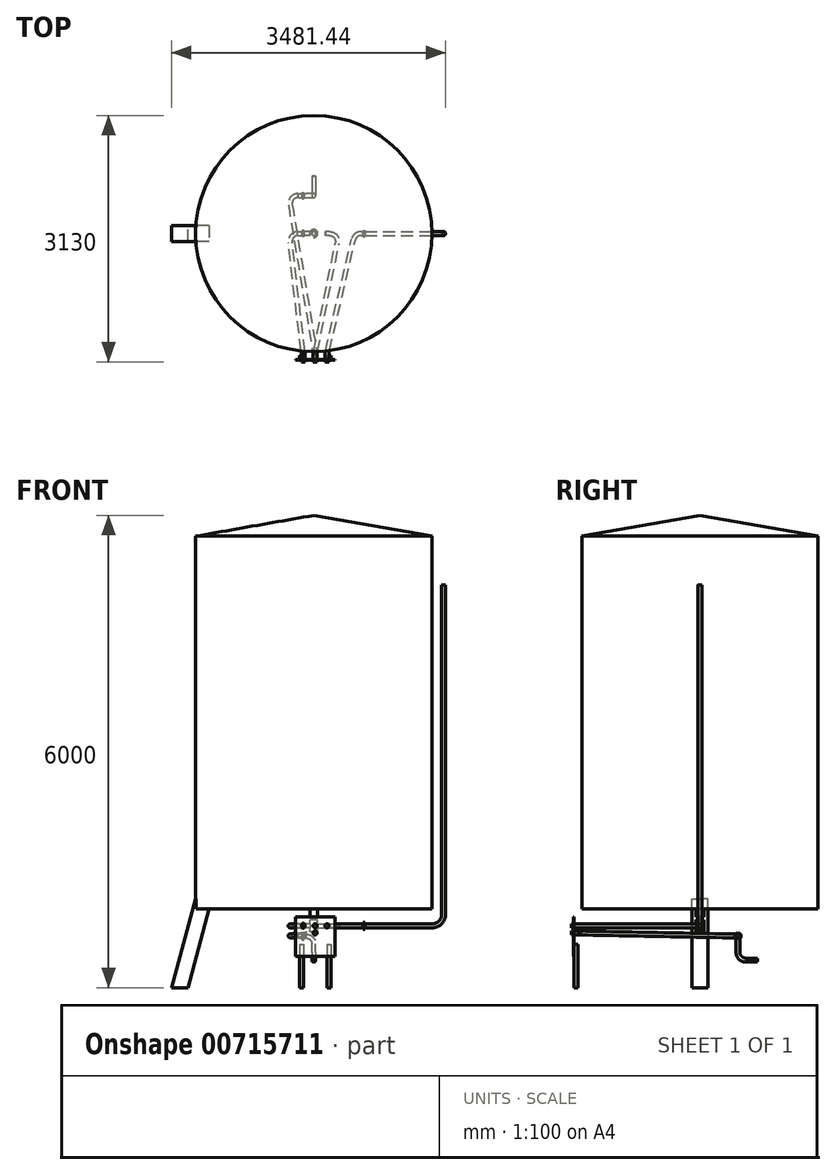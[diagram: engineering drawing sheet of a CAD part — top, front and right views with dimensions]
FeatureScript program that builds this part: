
annotation { "Feature Type Name" : "Feature", "Feature Type Description" : "" }
export const myFeature = defineFeature(function(context is Context, id is Id, definition is map)
    precondition{}
    {
        {
            var Q0;
            Q0=qCreatedBy(makeId("Front.planeOp"),FACE);
            var sketch = newSketch(context, id + "F0", { "sketchPlane" : qUnion([Q0])});
            skLineSegment(sketch, "E0", {"start": v(0, 5290) * mm, "end": v(0, 0) * mm});
            skLineSegment(sketch, "E1", {"start": v(0, 5290) * mm, "end": v(-1500, 5025.5) * mm});
            skLineSegment(sketch, "E2", {"start": v(-1500, 5025.5) * mm, "end": v(-1500, 290) * mm});
            skLineSegment(sketch, "E3", {"start": v(-1500, 290) * mm, "end": v(-50, 290) * mm});
            skLineSegment(sketch, "E4", {"start": v(-50, 290) * mm, "end": v(-50, 190) * mm});
            skLineSegment(sketch, "E5", {"start": v(-25, 190) * mm, "end": v(-50, 190) * mm});
            skLineSegment(sketch, "E6", {"start": v(-50, 0) * mm, "end": v(0, 0) * mm});
            skLineSegment(sketch, "E7", {"start": v(-50, 150) * mm, "end": v(-50, 0) * mm});
            skLineSegment(sketch, "E8", {"start": v(-25, 190) * mm, "end": v(-25, 150) * mm});
            skLineSegment(sketch, "E9", {"start": v(-25, 150) * mm, "end": v(-50, 150) * mm});
            skSolve(sketch);
        }
        {
            var Q0;
            Q0=makeQuery(id+"F0.imprint","IMPRINT",FACE,{"disambiguationData":[TD([[makeQuery(id+"F0.imprint","IMPRINT",EDGE,{"derivedFrom":sQuery(id+"F0.wireOp",EDGE,"E0")}),-1.0]])]});
            var Q1;
            Q1=sQuery(id+"F0.wireOp",EDGE,"E0");
            revolve(context, id + "F1", {"surfaceOperationType" : NewSurfaceOperationType.NEW, "entities" : qUnion([Q0]), "axis" : qUnion([Q1]), "revolveType" : RevolveType.FULL});
        }
        {
            var Q0;
            Q0=qCreatedBy(makeId("Front.planeOp"),FACE);
            var sketch = newSketch(context, id + "F2", { "sketchPlane" : qUnion([Q0])});
            skLineSegment(sketch, "E10", {"start": v(-1500, 5025.5) * mm, "end": v(-1500, 290) * mm, "construction": true});
            skLineSegment(sketch, "E11", {"start": v(1500, 290) * mm, "end": v(1500, 5025.5) * mm});
            skLineSegment(sketch, "E12", {"start": v(50, 290) * mm, "end": v(1500, 290) * mm});
            skLineSegment(sketch, "E13", {"start": v(-1500, 290) * mm, "end": v(-50, 290) * mm, "construction": true});
            skLineSegment(sketch, "E14", {"start": v(-1806.44, -710) * mm, "end": v(-1505, 415) * mm});
            skLineSegment(sketch, "E15", {"start": v(-1297.94, 415) * mm, "end": v(-1599.39, -710) * mm});
            skLineSegment(sketch, "E16", {"start": v(-1599.39, -710) * mm, "end": v(-1806.44, -710) * mm});
            skLineSegment(sketch, "E17", {"start": v(-1505, 415) * mm, "end": v(-1297.94, 415) * mm});
            skSolve(sketch);
        }
        {
            var Q0;
            Q0=makeQuery(id+"F2.imprint","IMPRINT",FACE,{"disambiguationData":[TD([[makeQuery(id+"F2.imprint","IMPRINT",EDGE,{"derivedFrom":sQuery(id+"F2.wireOp",EDGE,"E14")}),-1.0]])]});
            extrude(context, id + "F3", {"entities" : qUnion([Q0]), "operationType" : NewBodyOperationType.ADD, "endBound" : BoundingType.SYMMETRIC, "depth" : 200 * mm, "offsetDistance" : 25 * mm});
        }
        {
            var Q0;
            Q0=qCreatedBy(makeId("Right.planeOp"),FACE);
            cPlane(context, id + "F4", {"entities" : qUnion([Q0]), "cplaneType" : CPlaneType.OFFSET, "offset" : 150 * mm, "oppositeDirection" : true, "width" : 150 * mm, "height" : 150 * mm});
        }
        {
            var Q0;
            Q0=qCreatedBy(id+"F4.planeOp",FACE);
            var sketch = newSketch(context, id + "F5", { "sketchPlane" : qUnion([Q0])});
            skLineSegment(sketch, "E18", {"start": v(0, 0) * mm, "end": v(0, 150) * mm, "construction": true});
            skLineSegment(sketch, "E19.0", {"start": v(-50, 150) * mm, "end": v(50, 150) * mm, "construction": true});
            skLineSegment(sketch, "E20.0", {"start": v(-50, 0) * mm, "end": v(50, 0) * mm, "construction": true});
            skCircle(sketch, "E21", {"center": v(0, 75) * mm, "radius": 25 * mm});
            skCircle(sketch, "E22.cCircle", {"center": v(0, 75) * mm, "radius": 40 * mm, "construction": true});
            skLineSegment(sketch, "E22.0", {"start": v(-40, 51.9) * mm, "end": v(-40, 98.1) * mm});
            skLineSegment(sketch, "E22.1", {"start": v(-40, 98.1) * mm, "end": v(0, 121.19) * mm});
            skLineSegment(sketch, "E22.2", {"start": v(0, 121.19) * mm, "end": v(40, 98.1) * mm});
            skLineSegment(sketch, "E22.3", {"start": v(40, 98.1) * mm, "end": v(40, 51.9) * mm});
            skLineSegment(sketch, "E22.4", {"start": v(40, 51.9) * mm, "end": v(0, 28.81) * mm});
            skLineSegment(sketch, "E22.5", {"start": v(0, 28.81) * mm, "end": v(-40, 51.9) * mm});
            skPoint(sketch, "E22.0.midPoint", {"position": v(-40, 75) * mm});
            skSolve(sketch);
        }
        {
            var Q0;
            Q0=makeQuery(id+"F5.imprint","IMPRINT",FACE,{"disambiguationData":[TD([[makeQuery(id+"F5.imprint","IMPRINT",EDGE,{"derivedFrom":sQuery(id+"F5.wireOp",EDGE,"E21")}),-1.0]])]});
            var Q1;
            Q1=makeQuery(id+"F5.imprint","IMPRINT",FACE,{"disambiguationData":[TD([[makeQuery(id+"F5.imprint","IMPRINT",EDGE,{"derivedFrom":sQuery(id+"F5.wireOp",EDGE,"E21")}),1.0]])]});
            extrude(context, id + "F6", {"entities" : qUnion([Q0, Q1]), "depth" : 25 * mm, "offsetDistance" : 25 * mm});
        }
        {
            var Q0;
            Q0=makeQuery(id+"F5.imprint","IMPRINT",FACE,{"disambiguationData":[TD([[makeQuery(id+"F5.imprint","IMPRINT",EDGE,{"derivedFrom":sQuery(id+"F5.wireOp",EDGE,"E21")}),1.0]])]});
            var Q1;
            Q1=makeQuery(id+"F1.opRevolve","SWEPT_FACE",FACE,{"disambiguationData":[OSD([sQuery(id+"F0.wireOp",EDGE,"E7")])]});
            extrude(context, id + "F7", {"entities" : qUnion([Q0]), "operationType" : NewBodyOperationType.ADD, "endBound" : BoundingType.UP_TO_SURFACE, "depth" : 25 * mm, "endBoundEntityFace" : qUnion([Q1]), "offsetDistance" : 25 * mm});
        }
        {
            var Q0;
            Q0=qCreatedBy(makeId("Front.planeOp"),FACE);
            var sketch = newSketch(context, id + "F8", { "sketchPlane" : qUnion([Q0])});
            skLineSegment(sketch, "E23.0.0", {"start": v(150, 51.9) * mm, "end": v(150, 28.81) * mm, "construction": true});
            skLineSegment(sketch, "E23.0.1", {"start": v(150, 28.81) * mm, "end": v(150, 51.9) * mm, "construction": true});
            skLineSegment(sketch, "E23.0.2", {"start": v(150, 51.9) * mm, "end": v(150, 98.1) * mm, "construction": true});
            skLineSegment(sketch, "E23.0.3", {"start": v(150, 98.1) * mm, "end": v(150, 121.19) * mm, "construction": true});
            skLineSegment(sketch, "E23.0.4", {"start": v(150, 121.19) * mm, "end": v(150, 98.1) * mm, "construction": true});
            skLineSegment(sketch, "E23.0.5", {"start": v(150, 98.1) * mm, "end": v(150, 51.9) * mm, "construction": true});
            skLineSegment(sketch, "E24", {"start": v(150, 75) * mm, "end": v(650, 75) * mm, "construction": true});
            skLineSegment(sketch, "E25", {"start": v(1650, 225) * mm, "end": v(1650, 4408.12) * mm});
            skPoint(sketch, "E26.visualSharp", {"position": v(1650, 75) * mm});
            skArc(sketch, "E26.filletArc", {"start": v(1500, 75) * mm, "mid": v(1606.07, 118.93) * mm, "end": v(1650, 225) * mm});
            skPoint(sketch, "E27", {"position": v(650, 75) * mm});
            skLineSegment(sketch, "E28", {"start": v(650, 75) * mm, "end": v(1500, 75) * mm});
            skPoint(sketch, "E29", {"position": v(675, 75) * mm});
            skSolve(sketch);
        }
        {
            var Q0;
            Q0=makeQuery(id+"F7.opExtrude","SWEPT_FACE",FACE,{"disambiguationData":[OSD([sQuery(id+"F5.wireOp",EDGE,"E21")])]});
            var Q1;
            Q1=qCreatedBy(makeId("Top.planeOp"),FACE);
            cPlane(context, id + "F9", {"entities" : qUnion([Q0, Q1]), "cplaneType" : CPlaneType.LINE_ANGLE, "offset" : 25 * mm, "angle" : 15 * degree, "width" : 150 * mm, "height" : 150 * mm});
        }
        {
            var Q0;
            Q0=qCreatedBy(id+"F9.planeOp",FACE);
            var sketch = newSketch(context, id + "F10", { "sketchPlane" : qUnion([Q0])});
            skPoint(sketch, "E30.0", {"position": v(-150, 19.41) * mm});
            skLineSegment(sketch, "E31", {"start": v(-150, 19.41) * mm, "end": v(-400, 19.41) * mm});
            skLineSegment(sketch, "E32", {"start": v(-500, -80.59) * mm, "end": v(-500, -380.59) * mm});
            skLineSegment(sketch, "E33", {"start": v(-400, -480.59) * mm, "end": v(-375, -480.59) * mm});
            skPoint(sketch, "E34.visualSharp", {"position": v(-500, 19.41) * mm});
            skArc(sketch, "E34.filletArc", {"start": v(-400, 19.41) * mm, "mid": v(-470.71, -9.88) * mm, "end": v(-500, -80.59) * mm});
            skPoint(sketch, "E35.visualSharp", {"position": v(-500, -480.59) * mm});
            skArc(sketch, "E35.filletArc", {"start": v(-500, -380.59) * mm, "mid": v(-470.71, -451.3) * mm, "end": v(-400, -480.59) * mm});
            skSolve(sketch);
        }
        {
            var Q0;
            Q0=qCreatedBy(makeId("Front.planeOp"),FACE);
            var Q1;
            Q1=sQuery(id+"F10.wireOp",VERTEX,"E33.end");
            cPlane(context, id + "F11", {"entities" : qUnion([Q0, Q1]), "cplaneType" : CPlaneType.PLANE_POINT, "offset" : 25 * mm, "width" : 150 * mm, "height" : 150 * mm});
        }
        {
            var Q0;
            Q0=qCreatedBy(id+"F11.planeOp",FACE);
            var sketch = newSketch(context, id + "F12", { "sketchPlane" : qUnion([Q0])});
            skLineSegment(sketch, "E36", {"start": v(0, -154.4) * mm, "end": v(0, -204.4) * mm});
            skPoint(sketch, "E37.0", {"position": v(-375, -54.4) * mm});
            skLineSegment(sketch, "E38", {"start": v(-375, -54.4) * mm, "end": v(-125, -54.4) * mm, "construction": true});
            skPoint(sketch, "E39.visualSharp", {"position": v(0, -54.4) * mm});
            skArc(sketch, "E39.filletArc", {"start": v(0, -154.4) * mm, "mid": v(-29.29, -83.7) * mm, "end": v(-100, -54.4) * mm});
            skPoint(sketch, "E40", {"position": v(-125, -54.4) * mm});
            skLineSegment(sketch, "E41", {"start": v(-125, -54.4) * mm, "end": v(-100, -54.4) * mm});
            skSolve(sketch);
        }
        {
            var Q0;
            Q0=qCreatedBy(makeId("Right.planeOp"),FACE);
            var sketch = newSketch(context, id + "F13", { "sketchPlane" : qUnion([Q0])});
            skLineSegment(sketch, "E42", {"start": v(582.96, -360) * mm, "end": v(732.96, -360) * mm});
            skPoint(sketch, "E43.0", {"position": v(482.96, -204.4) * mm});
            skLineSegment(sketch, "E44", {"start": v(482.96, -204.4) * mm, "end": v(482.96, -260) * mm});
            skPoint(sketch, "E45.visualSharp", {"position": v(482.96, -360) * mm});
            skArc(sketch, "E45.filletArc", {"start": v(482.96, -260) * mm, "mid": v(512.25, -330.71) * mm, "end": v(582.96, -360) * mm});
            skSolve(sketch);
        }
        {
            var Q0;
            Q0=sQuery(id+"F13.wireOp",VERTEX,"E42.end");
            var Q1;
            Q1=sQuery(id+"F13.wireOp",EDGE,"E42");
            cPlane(context, id + "F14", {"entities" : qUnion([Q0, Q1]), "cplaneType" : CPlaneType.LINE_POINT, "offset" : 25 * mm, "width" : 150 * mm, "height" : 150 * mm});
        }
        {
            var Q0;
            Q0=qCreatedBy(id+"F14.planeOp",FACE);
            var sketch = newSketch(context, id + "F15", { "sketchPlane" : qUnion([Q0])});
            skCircle(sketch, "E46", {"center": v(0, -360) * mm, "radius": 25 * mm});
            skSolve(sketch);
        }
        {
            var Q0;
            Q0=sQuery(id+"F8.wireOp",VERTEX,"E25.end");
            var Q1;
            Q1=sQuery(id+"F8.wireOp",EDGE,"E25");
            cPlane(context, id + "F16", {"entities" : qUnion([Q0, Q1]), "cplaneType" : CPlaneType.LINE_POINT, "offset" : 25 * mm, "width" : 150 * mm, "height" : 150 * mm});
        }
        {
            var Q0;
            Q0=qCreatedBy(id+"F16.planeOp",FACE);
            var sketch = newSketch(context, id + "F17", { "sketchPlane" : qUnion([Q0])});
            skPoint(sketch, "E47.0", {"position": v(1650, 0) * mm});
            skCircle(sketch, "E48", {"center": v(1650, 0) * mm, "radius": 25 * mm});
            skSolve(sketch);
        }
        {
            var Q0;
            Q0=makeQuery(id+"F17.imprint","IMPRINT",FACE,{"disambiguationData":[TD([[makeQuery(id+"F17.imprint","IMPRINT",EDGE,{"derivedFrom":sQuery(id+"F17.wireOp",EDGE,"E48")}),1.0]])]});
            var Q1;
            Q1=sQuery(id+"F8.wireOp",EDGE,"E25");
            var Q2;
            Q2=sQuery(id+"F8.wireOp",EDGE,"E26.filletArc");
            var Q3;
            Q3=sQuery(id+"F8.wireOp",EDGE,"E24");
            sweep(context, id + "F18", {"operationType" : NewBodyOperationType.ADD, "profiles" : qUnion([Q0]), "path" : qUnion([Q1, Q2, Q3])});
        }
        {
            var Q0;
            Q0=makeQuery(id+"F15.imprint","IMPRINT",FACE,{"disambiguationData":[TD([[makeQuery(id+"F15.imprint","IMPRINT",EDGE,{"derivedFrom":sQuery(id+"F15.wireOp",EDGE,"E46")}),1.0]])]});
            var Q1;
            Q1=sQuery(id+"F13.wireOp",EDGE,"E42");
            var Q2;
            Q2=sQuery(id+"F13.wireOp",EDGE,"E45.filletArc");
            var Q3;
            Q3=sQuery(id+"F13.wireOp",EDGE,"E44");
            var Q4;
            Q4=sQuery(id+"F12.wireOp",EDGE,"E36");
            var Q5;
            Q5=sQuery(id+"F12.wireOp",EDGE,"E39.filletArc");
            sweep(context, id + "F19", {"operationType" : NewBodyOperationType.ADD, "profiles" : qUnion([Q0]), "path" : qUnion([Q1, Q2, Q3, Q4, Q5])});
        }
        {
            var Q0;
            Q0=sQuery(id+"F12.wireOp",VERTEX,"E40");
            var Q1;
            Q1=sQuery(id+"F12.wireOp",EDGE,"E38");
            cPlane(context, id + "F20", {"entities" : qUnion([Q0, Q1]), "cplaneType" : CPlaneType.LINE_POINT, "offset" : 25 * mm, "width" : 150 * mm, "height" : 150 * mm});
        }
        {
            var Q0;
            Q0=qCreatedBy(id+"F20.planeOp",FACE);
            var sketch = newSketch(context, id + "F21", { "sketchPlane" : qUnion([Q0])});
            skPoint(sketch, "E49.0", {"position": v(482.96, -54.4) * mm});
            skCircle(sketch, "E50.cCircle", {"center": v(482.96, -54.4) * mm, "radius": 40 * mm, "construction": true});
            skLineSegment(sketch, "E50.0", {"start": v(522.96, -31.32) * mm, "end": v(522.96, -77.5) * mm});
            skLineSegment(sketch, "E50.1", {"start": v(522.96, -77.5) * mm, "end": v(482.96, -100.6) * mm});
            skLineSegment(sketch, "E50.2", {"start": v(482.96, -100.6) * mm, "end": v(442.96, -77.5) * mm});
            skLineSegment(sketch, "E50.3", {"start": v(442.96, -77.5) * mm, "end": v(442.96, -31.32) * mm});
            skLineSegment(sketch, "E50.4", {"start": v(442.96, -31.32) * mm, "end": v(482.96, -8.22) * mm});
            skLineSegment(sketch, "E50.5", {"start": v(482.96, -8.22) * mm, "end": v(522.96, -31.32) * mm});
            skPoint(sketch, "E50.0.midPoint", {"position": v(522.96, -54.4) * mm});
            skSolve(sketch);
        }
        {
            var Q0;
            Q0=makeQuery(id+"F21.imprint","IMPRINT",FACE,{"disambiguationData":[TD([[makeQuery(id+"F21.imprint","IMPRINT",EDGE,{"derivedFrom":sQuery(id+"F21.wireOp",EDGE,"E50.0")}),-1.0]])]});
            extrude(context, id + "F22", {"entities" : qUnion([Q0]), "operationType" : NewBodyOperationType.ADD, "oppositeDirection" : true, "depth" : 25 * mm, "offsetDistance" : 25 * mm});
        }
        {
            var Q0;
            Q0=qCreatedBy(makeId("Front.planeOp"),FACE);
            cPlane(context, id + "F23", {"entities" : qUnion([Q0]), "cplaneType" : CPlaneType.OFFSET, "offset" : 1600 * mm, "width" : 150 * mm, "height" : 150 * mm});
        }
        {
            var Q0;
            Q0=qCreatedBy(id+"F23.planeOp",FACE);
            var sketch = newSketch(context, id + "F24", { "sketchPlane" : qUnion([Q0])});
            skLineSegment(sketch, "E51.bottom", {"start": v(-233.38, 190) * mm, "end": v(266.62, 190) * mm});
            skLineSegment(sketch, "E51.top", {"start": v(-233.38, -310) * mm, "end": v(266.62, -310) * mm});
            skLineSegment(sketch, "E51.left", {"start": v(-233.38, 190) * mm, "end": v(-233.38, -310) * mm});
            skLineSegment(sketch, "E51.right", {"start": v(266.62, 190) * mm, "end": v(266.62, -310) * mm});
            skLineSegment(sketch, "E52.bottom", {"start": v(-183.38, -160) * mm, "end": v(-133.38, -160) * mm});
            skLineSegment(sketch, "E52.top", {"start": v(-183.38, -710) * mm, "end": v(-133.38, -710) * mm});
            skLineSegment(sketch, "E52.left", {"start": v(-183.38, -160) * mm, "end": v(-183.38, -710) * mm});
            skLineSegment(sketch, "E52.right", {"start": v(-133.38, -160) * mm, "end": v(-133.38, -710) * mm});
            skLineSegment(sketch, "E53.bottom", {"start": v(166.62, -160) * mm, "end": v(216.62, -160) * mm});
            skLineSegment(sketch, "E53.top", {"start": v(166.62, -710) * mm, "end": v(216.62, -710) * mm});
            skLineSegment(sketch, "E53.left", {"start": v(166.62, -160) * mm, "end": v(166.62, -710) * mm});
            skLineSegment(sketch, "E53.right", {"start": v(216.62, -160) * mm, "end": v(216.62, -710) * mm});
            skSolve(sketch);
        }
        {
            var Q0;
            Q0=makeQuery(id+"F24.imprint","IMPRINT",FACE,{"disambiguationData":[TD([[makeQuery(id+"F24.imprint","IMPRINT",EDGE,{"derivedFrom":sQuery(id+"F24.wireOp",EDGE,"E51.bottom")}),-1.0]])]});
            var Q1;
            {var subQ5=sQuery(id+"F24.wireOp",EDGE,"E52.bottom");Q1=makeQuery(id+"F24.imprint","IMPRINT",FACE,{"disambiguationData":[TD([[makeQuery(id+"F24.imprint","IMPRINT",EDGE,{"derivedFrom":subQ5}),-1.0]])]});}
            var Q2;
            {var subQ5=sQuery(id+"F24.wireOp",EDGE,"E53.bottom");Q2=makeQuery(id+"F24.imprint","IMPRINT",FACE,{"disambiguationData":[TD([[makeQuery(id+"F24.imprint","IMPRINT",EDGE,{"derivedFrom":subQ5}),-1.0]])]});}
            extrude(context, id + "F25", {"entities" : qUnion([Q0, Q1, Q2]), "depth" : 5 * mm, "offsetDistance" : 25 * mm});
        }
        {
            var Q0;
            {var subQ5=sQuery(id+"F24.wireOp",EDGE,"E52.top");Q0=makeQuery(id+"F24.imprint","IMPRINT",FACE,{"disambiguationData":[TD([[makeQuery(id+"F24.imprint","IMPRINT",EDGE,{"derivedFrom":subQ5}),1.0]])]});}
            var Q1;
            {var subQ5=sQuery(id+"F24.wireOp",EDGE,"E53.top");Q1=makeQuery(id+"F24.imprint","IMPRINT",FACE,{"disambiguationData":[TD([[makeQuery(id+"F24.imprint","IMPRINT",EDGE,{"derivedFrom":subQ5}),1.0]])]});}
            var Q2;
            {var subQ5=sQuery(id+"F24.wireOp",EDGE,"E52.bottom");Q2=makeQuery(id+"F24.imprint","IMPRINT",FACE,{"disambiguationData":[TD([[makeQuery(id+"F24.imprint","IMPRINT",EDGE,{"derivedFrom":subQ5}),-1.0]])]});}
            var Q3;
            {var subQ5=sQuery(id+"F24.wireOp",EDGE,"E53.bottom");Q3=makeQuery(id+"F24.imprint","IMPRINT",FACE,{"disambiguationData":[TD([[makeQuery(id+"F24.imprint","IMPRINT",EDGE,{"derivedFrom":subQ5}),-1.0]])]});}
            extrude(context, id + "F26", {"entities" : qUnion([Q0, Q1, Q2, Q3]), "operationType" : NewBodyOperationType.ADD, "oppositeDirection" : true, "depth" : 50 * mm, "offsetDistance" : 25 * mm});
        }
        {
            var Q0;
            Q0=makeQuery(id+"F19.opSweep","CAP_FACE",FACE,{"disambiguationData":[OSD([sQuery(id+"F12.wireOp",VERTEX,"E39.filletArc.end"),sQuery(id+"F15.wireOp",EDGE,"E46")])],"isStart":false});
            extrude(context, id + "F27", {"entities" : qUnion([Q0]), "operationType" : NewBodyOperationType.ADD, "endBound" : BoundingType.UP_TO_NEXT, "depth" : 25 * mm, "offsetDistance" : 25 * mm});
        }
        {
            var Q0;
            Q0=qCreatedBy(makeId("Top.planeOp"),FACE);
            var Q1;
            Q1=sQuery(id+"F8.wireOp",VERTEX,"E27");
            cPlane(context, id + "F28", {"entities" : qUnion([Q0, Q1]), "cplaneType" : CPlaneType.PLANE_POINT, "offset" : 25 * mm, "width" : 150 * mm, "height" : 150 * mm});
        }
        {
            var Q0;
            Q0=qCreatedBy(id+"F28.planeOp",FACE);
            var sketch = newSketch(context, id + "F29", { "sketchPlane" : qUnion([Q0])});
            skPoint(sketch, "E54.0", {"position": v(650, 0) * mm});
            skLineSegment(sketch, "E55", {"start": v(650, 0) * mm, "end": v(600, 0) * mm});
            skLineSegment(sketch, "E56", {"start": v(502.61, -77.3) * mm, "end": v(169.23, -1507.3) * mm});
            skLineSegment(sketch, "E57.0", {"start": v(-233.38, -1600) * mm, "end": v(266.62, -1600) * mm, "construction": true});
            skLineSegment(sketch, "E58", {"start": v(166.62, -1630) * mm, "end": v(166.62, -1530) * mm});
            skPoint(sketch, "E59.visualSharp", {"position": v(166.62, -1518.5) * mm});
            skArc(sketch, "E59.filletArc", {"start": v(169.23, -1507.3) * mm, "mid": v(167.27, -1518.57) * mm, "end": v(166.62, -1530) * mm});
            skPoint(sketch, "E60.visualSharp", {"position": v(520.63, 0) * mm});
            skArc(sketch, "E60.filletArc", {"start": v(600, 0) * mm, "mid": v(537.83, -21.67) * mm, "end": v(502.61, -77.3) * mm});
            skLineSegment(sketch, "E61", {"start": v(16.62, -1630) * mm, "end": v(16.62, -1539.88) * mm});
            skLineSegment(sketch, "E62", {"start": v(18.55, -1520.31) * mm, "end": v(298.07, -119.57) * mm});
            skLineSegment(sketch, "E63", {"start": v(200, 0) * mm, "end": v(150, 0) * mm});
            skPoint(sketch, "E64.0", {"position": v(150, 0) * mm});
            skPoint(sketch, "E65.visualSharp", {"position": v(321.93, 0) * mm});
            skArc(sketch, "E65.filletArc", {"start": v(298.07, -119.57) * mm, "mid": v(277.32, -36.58) * mm, "end": v(200, 0) * mm});
            skPoint(sketch, "E66.0", {"position": v(-150, 0) * mm});
            skLineSegment(sketch, "E67", {"start": v(-150, 0) * mm, "end": v(-200, 0) * mm});
            skLineSegment(sketch, "E68", {"start": v(-299.32, -111.62) * mm, "end": v(-134.06, -1524.2) * mm});
            skLineSegment(sketch, "E69", {"start": v(-133.38, -1535.83) * mm, "end": v(-133.38, -1630) * mm});
            skPoint(sketch, "E70.visualSharp", {"position": v(-312.38, 0) * mm});
            skArc(sketch, "E70.filletArc", {"start": v(-200, 0) * mm, "mid": v(-274.7, -33.52) * mm, "end": v(-299.32, -111.62) * mm});
            skPoint(sketch, "E71.visualSharp", {"position": v(-133.38, -1530) * mm});
            skArc(sketch, "E71.filletArc", {"start": v(-133.38, -1535.83) * mm, "mid": v(-133.55, -1530) * mm, "end": v(-134.06, -1524.2) * mm});
            skPoint(sketch, "E72.visualSharp", {"position": v(16.62, -1530) * mm});
            skArc(sketch, "E72.filletArc", {"start": v(18.55, -1520.31) * mm, "mid": v(17.1, -1530.05) * mm, "end": v(16.62, -1539.88) * mm});
            skSolve(sketch);
        }
        {
            var Q0;
            Q0=makeQuery(id+"F25.opExtrude","CAP_FACE",FACE,{"disambiguationData":[OSD([sQuery(id+"F24.wireOp",EDGE,"E51.bottom"),sQuery(id+"F24.wireOp",EDGE,"E51.top"),sQuery(id+"F24.wireOp",EDGE,"E51.left"),sQuery(id+"F24.wireOp",EDGE,"E51.right")])],"isStart":false});
            cPlane(context, id + "F30", {"entities" : qUnion([Q0]), "cplaneType" : CPlaneType.OFFSET, "offset" : 25 * mm, "width" : 150 * mm, "height" : 150 * mm});
        }
        {
            var Q0;
            Q0=qCreatedBy(id+"F30.planeOp",FACE);
            var sketch = newSketch(context, id + "F31", { "sketchPlane" : qUnion([Q0])});
            skPoint(sketch, "E73.0", {"position": v(-133.38, 75) * mm});
            skPoint(sketch, "E74.0", {"position": v(16.62, 75) * mm});
            skPoint(sketch, "E75.0", {"position": v(166.62, 75) * mm});
            skPoint(sketch, "E76", {"position": v(16.62, -15.14) * mm});
            skCircle(sketch, "E77", {"center": v(-133.38, 75) * mm, "radius": 25 * mm});
            skCircle(sketch, "E78", {"center": v(16.62, -15.14) * mm, "radius": 25 * mm});
            skCircle(sketch, "E79", {"center": v(16.62, 75) * mm, "radius": 25 * mm});
            skCircle(sketch, "E80", {"center": v(166.62, 75) * mm, "radius": 25 * mm});
            skSolve(sketch);
        }
        {
            var Q0;
            Q0=makeQuery(id+"F31.imprint","IMPRINT",FACE,{"disambiguationData":[TD([[makeQuery(id+"F31.imprint","IMPRINT",EDGE,{"derivedFrom":sQuery(id+"F31.wireOp",EDGE,"E78")}),1.0]])]});
            var Q1;
            Q1=sQuery(id+"F29.wireOp",VERTEX,"E72.filletArc.end");
            extrude(context, id + "F32", {"entities" : qUnion([Q0]), "operationType" : NewBodyOperationType.ADD, "endBound" : BoundingType.UP_TO_VERTEX, "oppositeDirection" : true, "depth" : 25 * mm, "endBoundEntityVertex" : qUnion([Q1]), "offsetDistance" : 25 * mm});
        }
        {
            var Q0;
            Q0=makeQuery(id+"F32.opExtrude","CAP_FACE",FACE,{"disambiguationData":[OSD([sQuery(id+"F31.wireOp",EDGE,"E78")])],"isStart":false});
            var sketch = newSketch(context, id + "F33", { "sketchPlane" : qUnion([Q0])});
            skCircle(sketch, "E81.0", {"center": v(-16.62, -15.14) * mm, "radius": 25 * mm});
            skSolve(sketch);
        }
        {
            var Q0;
            Q0=sQuery(id+"F33.wireOp",VERTEX,"E81.0.center");
            var Q1;
            Q1=sQuery(id+"F12.wireOp",VERTEX,"E37.0");
            var Q2;
            Q2=sQuery(id+"F12.wireOp",VERTEX,"E40");
            cPlane(context, id + "F34", {"entities" : qUnion([Q0, Q1, Q2]), "cplaneType" : CPlaneType.THREE_POINT, "offset" : 25 * mm, "width" : 150 * mm, "height" : 150 * mm});
        }
        {
            var Q0;
            Q0=qCreatedBy(id+"F34.planeOp",FACE);
            var sketch = newSketch(context, id + "F35", { "sketchPlane" : qUnion([Q0])});
            skLineSegment(sketch, "E82.0.0", {"start": v(-150, 483.03) * mm, "end": v(-150, 523.47) * mm, "construction": true});
            skLineSegment(sketch, "E82.0.1", {"start": v(-150, 523.47) * mm, "end": v(-150, 524.37) * mm, "construction": true});
            skLineSegment(sketch, "E82.0.2", {"start": v(-150, 524.37) * mm, "end": v(-150, 484.82) * mm, "construction": true});
            skLineSegment(sketch, "E82.0.3", {"start": v(-150, 484.82) * mm, "end": v(-150, 444.38) * mm, "construction": true});
            skLineSegment(sketch, "E82.0.4", {"start": v(-150, 444.38) * mm, "end": v(-150, 443.49) * mm, "construction": true});
            skLineSegment(sketch, "E82.0.5", {"start": v(-150, 443.49) * mm, "end": v(-150, 483.03) * mm, "construction": true});
            skPoint(sketch, "E83.0", {"position": v(16.62, -1539.3) * mm});
            skLineSegment(sketch, "E84", {"start": v(-150, 483.03) * mm, "end": v(-200, 483.03) * mm});
            skLineSegment(sketch, "E85", {"start": v(-298.65, 366.64) * mm, "end": v(15.27, -1522.9) * mm});
            skPoint(sketch, "E86.visualSharp", {"position": v(-317.98, 483.03) * mm});
            skArc(sketch, "E86.filletArc", {"start": v(-200, 483.03) * mm, "mid": v(-276.29, 447.69) * mm, "end": v(-298.65, 366.64) * mm});
            skLineSegment(sketch, "E87", {"start": v(16.62, -1539.3) * mm, "end": v(16.62, -1489.3) * mm, "construction": true});
            skArc(sketch, "E88", {"start": v(16.62, -1539.3) * mm, "mid": v(16.28, -1531.07) * mm, "end": v(15.27, -1522.9) * mm});
            skSolve(sketch);
        }
        {
            var Q0;
            Q0=makeQuery(id+"F33.imprint","IMPRINT",FACE,{"disambiguationData":[TD([[makeQuery(id+"F33.imprint","IMPRINT",EDGE,{"derivedFrom":sQuery(id+"F33.wireOp",EDGE,"E81.0")}),-1.0]])]});
            var Q1;
            Q1=sQuery(id+"F35.wireOp",EDGE,"E88");
            var Q2;
            Q2=sQuery(id+"F35.wireOp",EDGE,"E85");
            var Q3;
            Q3=sQuery(id+"F35.wireOp",EDGE,"E86.filletArc");
            var Q4;
            Q4=sQuery(id+"F35.wireOp",EDGE,"E84");
            sweep(context, id + "F36", {"operationType" : NewBodyOperationType.ADD, "profiles" : qUnion([Q0]), "path" : qUnion([Q1, Q2, Q3, Q4])});
        }
        {
            var Q0;
            Q0=makeQuery(id+"F31.imprint","IMPRINT",FACE,{"disambiguationData":[TD([[makeQuery(id+"F31.imprint","IMPRINT",EDGE,{"derivedFrom":sQuery(id+"F31.wireOp",EDGE,"E77")}),1.0]])]});
            var Q1;
            Q1=sQuery(id+"F29.wireOp",EDGE,"E69");
            var Q2;
            Q2=sQuery(id+"F29.wireOp",EDGE,"E71.filletArc");
            var Q3;
            Q3=sQuery(id+"F29.wireOp",EDGE,"E68");
            var Q4;
            Q4=sQuery(id+"F29.wireOp",EDGE,"E70.filletArc");
            var Q5;
            Q5=sQuery(id+"F29.wireOp",EDGE,"E67");
            sweep(context, id + "F37", {"operationType" : NewBodyOperationType.ADD, "profiles" : qUnion([Q0]), "path" : qUnion([Q1, Q2, Q3, Q4, Q5])});
        }
        {
            var Q0;
            Q0=makeQuery(id+"F31.imprint","IMPRINT",FACE,{"disambiguationData":[TD([[makeQuery(id+"F31.imprint","IMPRINT",EDGE,{"derivedFrom":sQuery(id+"F31.wireOp",EDGE,"E79")}),1.0]])]});
            var Q1;
            Q1=sQuery(id+"F29.wireOp",EDGE,"E61");
            var Q2;
            Q2=sQuery(id+"F29.wireOp",EDGE,"E72.filletArc");
            var Q3;
            Q3=sQuery(id+"F29.wireOp",EDGE,"E62");
            var Q4;
            Q4=sQuery(id+"F29.wireOp",EDGE,"E65.filletArc");
            var Q5;
            Q5=sQuery(id+"F29.wireOp",EDGE,"E63");
            sweep(context, id + "F38", {"operationType" : NewBodyOperationType.ADD, "profiles" : qUnion([Q0]), "path" : qUnion([Q1, Q2, Q3, Q4, Q5])});
        }
        {
            var Q0;
            Q0=makeQuery(id+"F31.imprint","IMPRINT",FACE,{"disambiguationData":[TD([[makeQuery(id+"F31.imprint","IMPRINT",EDGE,{"derivedFrom":sQuery(id+"F31.wireOp",EDGE,"E80")}),1.0]])]});
            var Q1;
            Q1=sQuery(id+"F29.wireOp",EDGE,"E58");
            var Q2;
            Q2=sQuery(id+"F29.wireOp",EDGE,"E59.filletArc");
            var Q3;
            Q3=sQuery(id+"F29.wireOp",EDGE,"E56");
            var Q4;
            Q4=sQuery(id+"F29.wireOp",EDGE,"E60.filletArc");
            var Q5;
            Q5=sQuery(id+"F29.wireOp",EDGE,"E55");
            var Q6;
            Q6=sQuery(id+"F8.wireOp",EDGE,"E28");
            sweep(context, id + "F39", {"operationType" : NewBodyOperationType.ADD, "profiles" : qUnion([Q0]), "path" : qUnion([Q1, Q2, Q3, Q4, Q5, Q6])});
        }
        {
            var Q0;
            Q0=sQuery(id+"F8.wireOp",EDGE,"E28");
            var Q1;
            Q1=sQuery(id+"F8.wireOp",VERTEX,"E27");
            cPlane(context, id + "F40", {"entities" : qUnion([Q0, Q1]), "cplaneType" : CPlaneType.LINE_POINT, "offset" : 25 * mm, "width" : 150 * mm, "height" : 150 * mm});
        }
        {
            var Q0;
            Q0=qCreatedBy(id+"F40.planeOp",FACE);
            var sketch = newSketch(context, id + "F41", { "sketchPlane" : qUnion([Q0])});
            skPoint(sketch, "E89.0", {"position": v(0, 75) * mm});
            skCircle(sketch, "E90.cCircle", {"center": v(0, 75) * mm, "radius": 40 * mm, "construction": true});
            skLineSegment(sketch, "E90.0", {"start": v(-40, 51.9) * mm, "end": v(-40, 98.1) * mm});
            skLineSegment(sketch, "E90.1", {"start": v(-40, 98.1) * mm, "end": v(0, 121.19) * mm});
            skLineSegment(sketch, "E90.2", {"start": v(0, 121.19) * mm, "end": v(40, 98.1) * mm});
            skLineSegment(sketch, "E90.3", {"start": v(40, 98.1) * mm, "end": v(40, 51.9) * mm});
            skLineSegment(sketch, "E90.4", {"start": v(40, 51.9) * mm, "end": v(0, 28.81) * mm});
            skLineSegment(sketch, "E90.5", {"start": v(0, 28.81) * mm, "end": v(-40, 51.9) * mm});
            skPoint(sketch, "E90.0.midPoint", {"position": v(-40, 75) * mm});
            skSolve(sketch);
        }
        {
            var Q0;
            Q0=makeQuery(id+"F41.imprint","IMPRINT",FACE,{"disambiguationData":[TD([[makeQuery(id+"F41.imprint","IMPRINT",EDGE,{"derivedFrom":sQuery(id+"F41.wireOp",EDGE,"E90.0")}),-1.0]])]});
            extrude(context, id + "F42", {"entities" : qUnion([Q0]), "operationType" : NewBodyOperationType.ADD, "oppositeDirection" : true, "depth" : 25 * mm, "offsetDistance" : 25 * mm});
        }
    });
